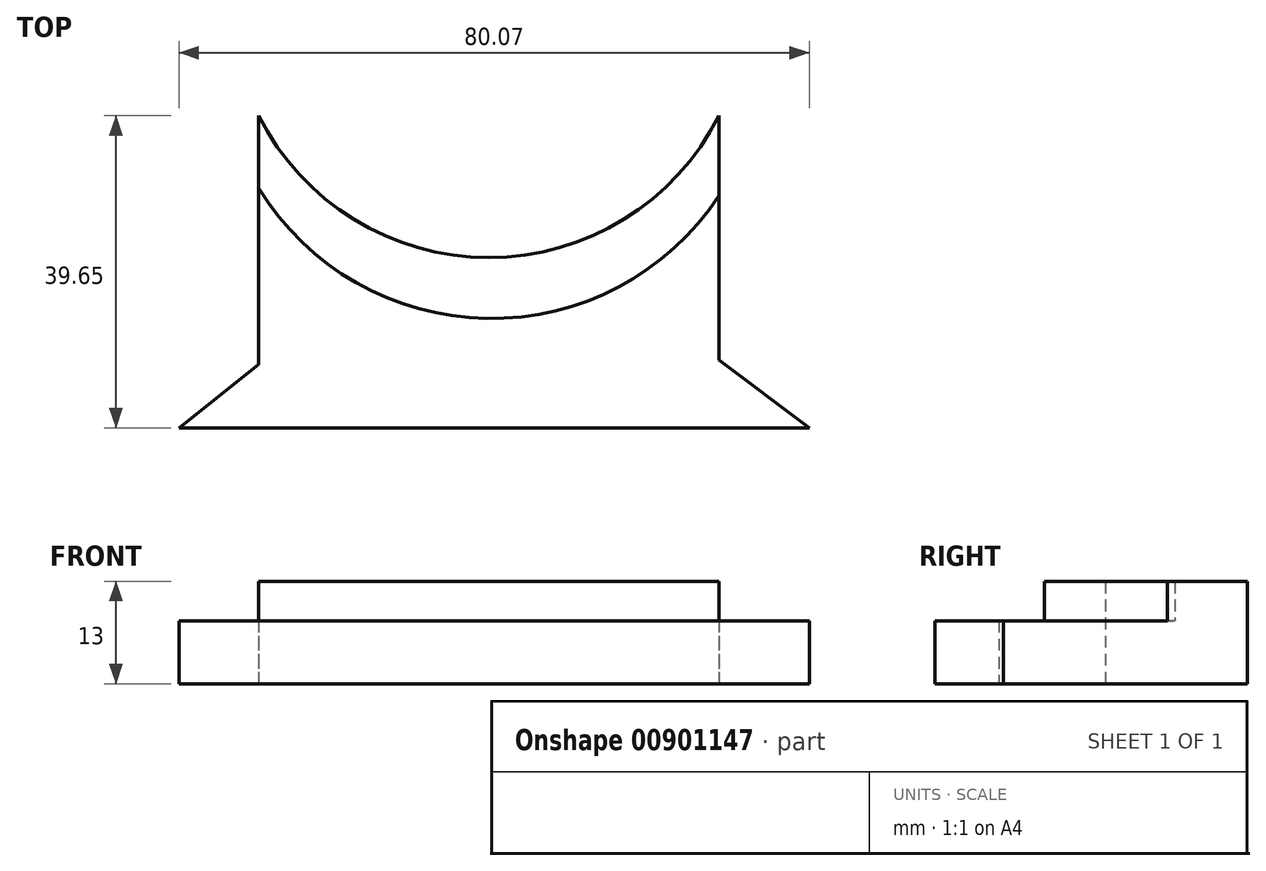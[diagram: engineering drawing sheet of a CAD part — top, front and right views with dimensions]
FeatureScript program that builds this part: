
annotation { "Feature Type Name" : "Feature", "Feature Type Description" : "" }
export const myFeature = defineFeature(function(context is Context, id is Id, definition is map)
    precondition{}
    {
        {
            var Q0;
            Q0=qCreatedBy(makeId("Top.planeOp"),FACE);
            var sketch = newSketch(context, id + "F0", { "sketchPlane" : qUnion([Q0])});
            skLineSegment(sketch, "E0", {"start": v(-45.58, -2.91) * mm, "end": v(-45.58, 28.66) * mm});
            skLineSegment(sketch, "E1", {"start": v(-45.58, 28.66) * mm, "end": v(12.87, 28.66) * mm});
            skLineSegment(sketch, "E2", {"start": v(12.87, 28.66) * mm, "end": v(12.87, -2.35) * mm});
            skLineSegment(sketch, "E3", {"start": v(12.87, -2.35) * mm, "end": v(24.34, -11) * mm});
            skLineSegment(sketch, "E4", {"start": v(24.34, -11) * mm, "end": v(-55.73, -11) * mm});
            skLineSegment(sketch, "E5", {"start": v(-55.73, -11) * mm, "end": v(-45.58, -2.91) * mm});
            skSolve(sketch);
        }
        {
            var Q0;
            Q0 = qSketchRegion(id + "F0", true);
            extrude(context, id + "F1", {"entities" : qUnion([Q0]), "depth" : 8 * mm, "offsetDistance" : 25 * mm});
        }
        {
            var Q0;
            Q0=makeQuery(id+"F1.opExtrude","CAP_FACE",FACE,{"disambiguationData":[OSD([sQuery(id+"F0.wireOp",EDGE,"E0"),sQuery(id+"F0.wireOp",EDGE,"E1"),sQuery(id+"F0.wireOp",EDGE,"E2"),sQuery(id+"F0.wireOp",EDGE,"E3"),sQuery(id+"F0.wireOp",EDGE,"E4"),sQuery(id+"F0.wireOp",EDGE,"E5")])],"isStart":true});
            var sketch = newSketch(context, id + "F2", { "sketchPlane" : qUnion([Q0])});
            skArc(sketch, "E6", {"start": v(12.87, -28.66) * mm, "mid": v(-16.35, -10.65) * mm, "end": v(-45.58, -28.66) * mm});
            skSolve(sketch);
        }
        {
            var Q0;
            Q0 = qSketchRegion(id + "F2", true);
            var Q1;
            Q1=makeQuery(id+"F2.imprint","IMPRINT",FACE,{"disambiguationData":[TD([[makeQuery(id+"F2.imprint","IMPRINT",EDGE,{"derivedFrom":sQuery(id+"F2.wireOp",EDGE,"E6")}),1.0]])]});
            extrude(context, id + "F3", {"entities" : qUnion([Q0, Q1]), "operationType" : NewBodyOperationType.REMOVE, "oppositeDirection" : true, "depth" : 25 * mm, "offsetDistance" : 25 * mm, "hasSecondDirection" : true, "secondDirectionOppositeDirection" : false, "secondDirectionDepth" : 25 * mm});
        }
        {
            var Q0;
            Q0=makeQuery(id+"F1.opExtrude","CAP_FACE",FACE,{"disambiguationData":[OSD([sQuery(id+"F0.wireOp",EDGE,"E0"),sQuery(id+"F0.wireOp",EDGE,"E1"),sQuery(id+"F0.wireOp",EDGE,"E2"),sQuery(id+"F0.wireOp",EDGE,"E3"),sQuery(id+"F0.wireOp",EDGE,"E4"),sQuery(id+"F0.wireOp",EDGE,"E5")])],"isStart":false});
            var sketch = newSketch(context, id + "F4", { "sketchPlane" : qUnion([Q0])});
            skArc(sketch, "E7", {"start": v(-45.58, 19.45) * mm, "mid": v(-16.61, 2.9) * mm, "end": v(12.87, 18.5) * mm});
            skSolve(sketch);
        }
        {
            var Q0;
            {var subQ0=sQuery(id+"F4.wireOp",EDGE,"E7");Q0=makeQuery(id+"F4.imprint","IMPRINT",FACE,{"disambiguationData":[TD([[makeQuery(id+"F4.imprint","IMPRINT",EDGE,{"derivedFrom":subQ0}),1.0]])]});}
            extrude(context, id + "F5", {"entities" : qUnion([Q0]), "operationType" : NewBodyOperationType.ADD, "depth" : 5 * mm, "offsetDistance" : 25 * mm});
        }
    });
